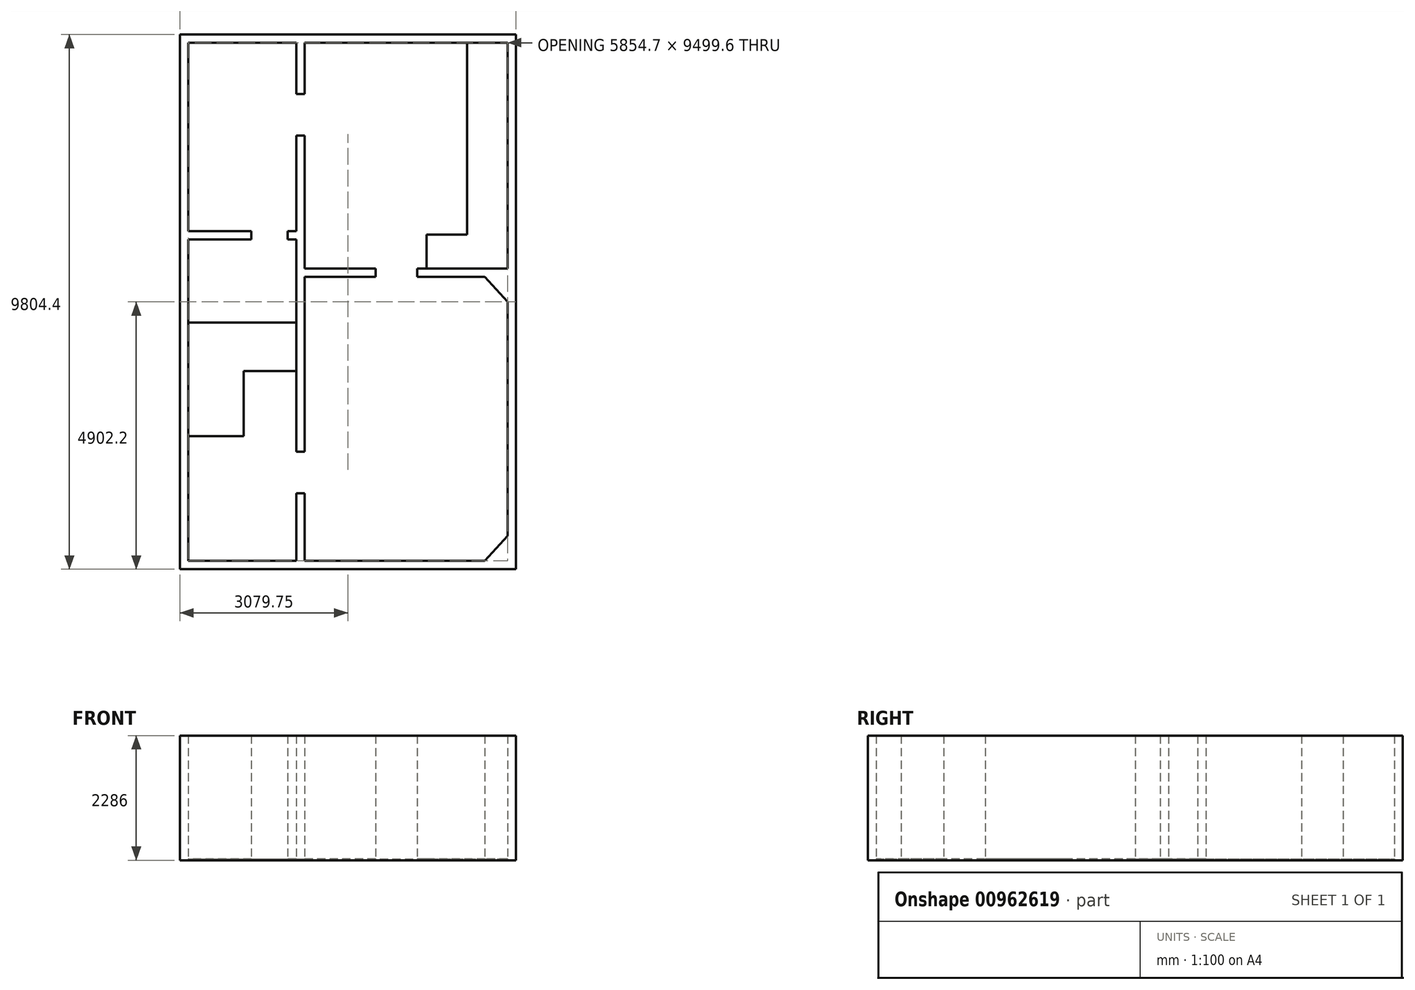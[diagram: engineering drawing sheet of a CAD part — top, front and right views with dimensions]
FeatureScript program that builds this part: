
annotation { "Feature Type Name" : "Feature", "Feature Type Description" : "" }
export const myFeature = defineFeature(function(context is Context, id is Id, definition is map)
    precondition{}
    {
        {
            var Q0;
            Q0=qCreatedBy(makeId("Top.planeOp"),FACE);
            var sketch = newSketch(context, id + "F0", { "sketchPlane" : qUnion([Q0])});
            skLineSegment(sketch, "E0", {"start": v(5434.25, 0) * mm, "end": v(5854.7, 458.64) * mm});
            skLineSegment(sketch, "E1", {"start": v(0, 2286) * mm, "end": v(1016, 2286) * mm});
            skLineSegment(sketch, "E2", {"start": v(1016, 2286) * mm, "end": v(1016, 3479.8) * mm});
            skLineSegment(sketch, "E3", {"start": v(0, 9499.6) * mm, "end": v(1981.2, 9499.6) * mm});
            skLineSegment(sketch, "E4", {"start": v(0, 0) * mm, "end": v(1981.2, 0) * mm});
            skLineSegment(sketch, "E5", {"start": v(0, 0) * mm, "end": v(0, 5892.8) * mm});
            skLineSegment(sketch, "E6", {"start": v(5854.7, 4749.8) * mm, "end": v(5439.36, 5207) * mm});
            skLineSegment(sketch, "E7.0", {"start": v(1157.63, 6045.2) * mm, "end": v(0, 6045.2) * mm});
            skLineSegment(sketch, "E8.0", {"start": v(1157.63, 5892.8) * mm, "end": v(0, 5892.8) * mm});
            skLineSegment(sketch, "E9.0", {"start": v(1981.2, 6045.2) * mm, "end": v(1824.83, 6045.2) * mm});
            skLineSegment(sketch, "E10.0", {"start": v(1981.2, 5892.8) * mm, "end": v(1824.83, 5892.8) * mm});
            skLineSegment(sketch, "E11.0", {"start": v(2133.6, 5969) * mm, "end": v(2133.6, 7797.8) * mm});
            skLineSegment(sketch, "E12.0", {"start": v(1981.2, 6045.2) * mm, "end": v(1981.2, 7797.8) * mm});
            skLineSegment(sketch, "E13.0", {"start": v(2133.6, 5359.4) * mm, "end": v(2133.6, 5969) * mm});
            skLineSegment(sketch, "E14.0", {"start": v(1981.2, 5283.2) * mm, "end": v(1981.2, 5892.8) * mm});
            skLineSegment(sketch, "E15.0", {"start": v(3435.35, 5359.4) * mm, "end": v(2133.6, 5359.4) * mm});
            skLineSegment(sketch, "E16.0", {"start": v(3435.35, 5207) * mm, "end": v(2133.6, 5207) * mm});
            skLineSegment(sketch, "E17.0", {"start": v(5854.7, 5359.4) * mm, "end": v(4197.35, 5359.4) * mm});
            skLineSegment(sketch, "E18.0", {"start": v(5854.7, 5207) * mm, "end": v(5848.35, 5207) * mm});
            skLineSegment(sketch, "E19.0", {"start": v(6007.1, 0) * mm, "end": v(6007.1, 9499.6) * mm});
            skLineSegment(sketch, "E20.0", {"start": v(0, 9652) * mm, "end": v(5854.7, 9652) * mm});
            skLineSegment(sketch, "E21.0", {"start": v(-152.4, 0) * mm, "end": v(-152.4, 9499.6) * mm});
            skLineSegment(sketch, "E22.0", {"start": v(1981.2, 5283.2) * mm, "end": v(1981.2, 4368.8) * mm});
            skLineSegment(sketch, "E23.0", {"start": v(2133.6, 5207) * mm, "end": v(2133.6, 4368.8) * mm});
            skLineSegment(sketch, "E24.0", {"start": v(2133.6, 8559.8) * mm, "end": v(2133.6, 9499.6) * mm});
            skLineSegment(sketch, "E25.0", {"start": v(1981.2, 8559.8) * mm, "end": v(1981.2, 9499.6) * mm});
            skLineSegment(sketch, "E26.0", {"start": v(0, -152.4) * mm, "end": v(5854.7, -152.4) * mm});
            skLineSegment(sketch, "E27.0", {"start": v(1981.2, 1238.25) * mm, "end": v(1981.2, 0) * mm});
            skLineSegment(sketch, "E28.0", {"start": v(2133.6, 1238.25) * mm, "end": v(2133.6, 0) * mm});
            skLineSegment(sketch, "E29.0", {"start": v(1981.2, 3479.8) * mm, "end": v(1981.2, 2000.25) * mm});
            skLineSegment(sketch, "E30.0", {"start": v(2133.6, 3479.8) * mm, "end": v(2133.6, 2000.25) * mm});
            skLineSegment(sketch, "E31", {"start": v(0, 4368.8) * mm, "end": v(1981.2, 4368.8) * mm});
            skLineSegment(sketch, "E32", {"start": v(1016, 3479.8) * mm, "end": v(1981.2, 3479.8) * mm});
            skLineSegment(sketch, "E33", {"start": v(3435.35, 5359.4) * mm, "end": v(3435.35, 5207) * mm});
            skLineSegment(sketch, "E34", {"start": v(1981.2, 7797.8) * mm, "end": v(2133.6, 7797.8) * mm});
            skLineSegment(sketch, "E35", {"start": v(1824.83, 6045.2) * mm, "end": v(1824.83, 5892.8) * mm});
            skLineSegment(sketch, "E36", {"start": v(1157.63, 6045.2) * mm, "end": v(1157.63, 5892.8) * mm});
            skLineSegment(sketch, "E37", {"start": v(4197.35, 5359.4) * mm, "end": v(4197.35, 5207) * mm});
            skLineSegment(sketch, "E38", {"start": v(2133.6, 4368.8) * mm, "end": v(2133.6, 3479.8) * mm});
            skLineSegment(sketch, "E39", {"start": v(1981.2, 1238.25) * mm, "end": v(2133.6, 1238.25) * mm});
            skLineSegment(sketch, "E40", {"start": v(1981.2, 2000.25) * mm, "end": v(2133.6, 2000.25) * mm});
            skLineSegment(sketch, "E41.trimOffspring", {"start": v(5439.36, 5207) * mm, "end": v(4197.35, 5207) * mm});
            skLineSegment(sketch, "E42.trimOffspring", {"start": v(5848.35, 5359.4) * mm, "end": v(5848.35, 9499.6) * mm});
            skLineSegment(sketch, "E43.trimOffspring", {"start": v(5854.7, 5359.4) * mm, "end": v(5854.7, 9499.6) * mm});
            skLineSegment(sketch, "E44", {"start": v(6007.1, 0) * mm, "end": v(6007.1, -152.4) * mm});
            skLineSegment(sketch, "E45", {"start": v(6007.1, -152.4) * mm, "end": v(5854.7, -152.4) * mm});
            skLineSegment(sketch, "E46", {"start": v(-152.4, 0) * mm, "end": v(-152.4, -152.4) * mm});
            skLineSegment(sketch, "E47", {"start": v(-152.4, -152.4) * mm, "end": v(0, -152.4) * mm});
            skLineSegment(sketch, "E48", {"start": v(0, 9652) * mm, "end": v(-152.4, 9652) * mm});
            skLineSegment(sketch, "E49", {"start": v(-152.4, 9652) * mm, "end": v(-152.4, 9499.6) * mm});
            skLineSegment(sketch, "E50", {"start": v(5854.7, 9652) * mm, "end": v(6007.1, 9652) * mm});
            skLineSegment(sketch, "E51", {"start": v(6007.1, 9652) * mm, "end": v(6007.1, 9499.6) * mm});
            skLineSegment(sketch, "E52.trimOffspring", {"start": v(2133.6, 9499.6) * mm, "end": v(5854.7, 9499.6) * mm});
            skLineSegment(sketch, "E53", {"start": v(5854.7, 4749.8) * mm, "end": v(5854.7, 458.64) * mm});
            skPoint(sketch, "E54.orphan", {"position": v(5854.7, 0) * mm});
            skLineSegment(sketch, "E55.trimOffspring", {"start": v(0, 6045.2) * mm, "end": v(0, 9499.6) * mm});
            skLineSegment(sketch, "E56", {"start": v(4372.64, 5359.4) * mm, "end": v(4372.64, 5983.5) * mm});
            skLineSegment(sketch, "E57", {"start": v(4372.64, 5983.5) * mm, "end": v(5113.67, 5983.5) * mm});
            skLineSegment(sketch, "E58", {"start": v(5113.67, 5983.5) * mm, "end": v(5113.67, 9499.6) * mm});
            skLineSegment(sketch, "E59.trimOffspring", {"start": v(5848.35, 5983.5) * mm, "end": v(5854.7, 5983.5) * mm});
            skLineSegment(sketch, "E60", {"start": v(1981.2, 4368.8) * mm, "end": v(1981.2, 3479.8) * mm});
            skLineSegment(sketch, "E61", {"start": v(1981.2, 8559.8) * mm, "end": v(2133.6, 8559.8) * mm});
            skLineSegment(sketch, "E62.trimOffspring", {"start": v(2133.6, 0) * mm, "end": v(5434.25, 0) * mm});
            skSolve(sketch);
        }
        {
            var Q0;
            Q0=makeQuery(id+"F0.imprint","IMPRINT",FACE,{"disambiguationData":[TD([[makeQuery(id+"F0.imprint","IMPRINT",EDGE,{"derivedFrom":sQuery(id+"F0.wireOp",EDGE,"E0")}),-1.0]])]});
            var Q1;
            Q1=makeQuery(id+"F0.imprint","IMPRINT",FACE,{"disambiguationData":[TD([[makeQuery(id+"F0.imprint","IMPRINT",EDGE,{"derivedFrom":sQuery(id+"F0.wireOp",EDGE,"E9.0")}),1.0]])]});
            extrude(context, id + "F1", {"entities" : qUnion([Q0, Q1]), "depth" : 2286 * mm, "offsetDistance" : 25.4 * mm});
        }
        {
            var Q0;
            Q0=makeQuery(id+"F0.imprint","IMPRINT",FACE,{"disambiguationData":[TD([[makeQuery(id+"F0.imprint","IMPRINT",EDGE,{"derivedFrom":sQuery(id+"F0.wireOp",EDGE,"E0")}),1.0]])]});
            extrude(context, id + "F2", {"entities" : qUnion([Q0]), "depth" : 25.4 * mm, "offsetDistance" : 25.4 * mm});
        }
    });
